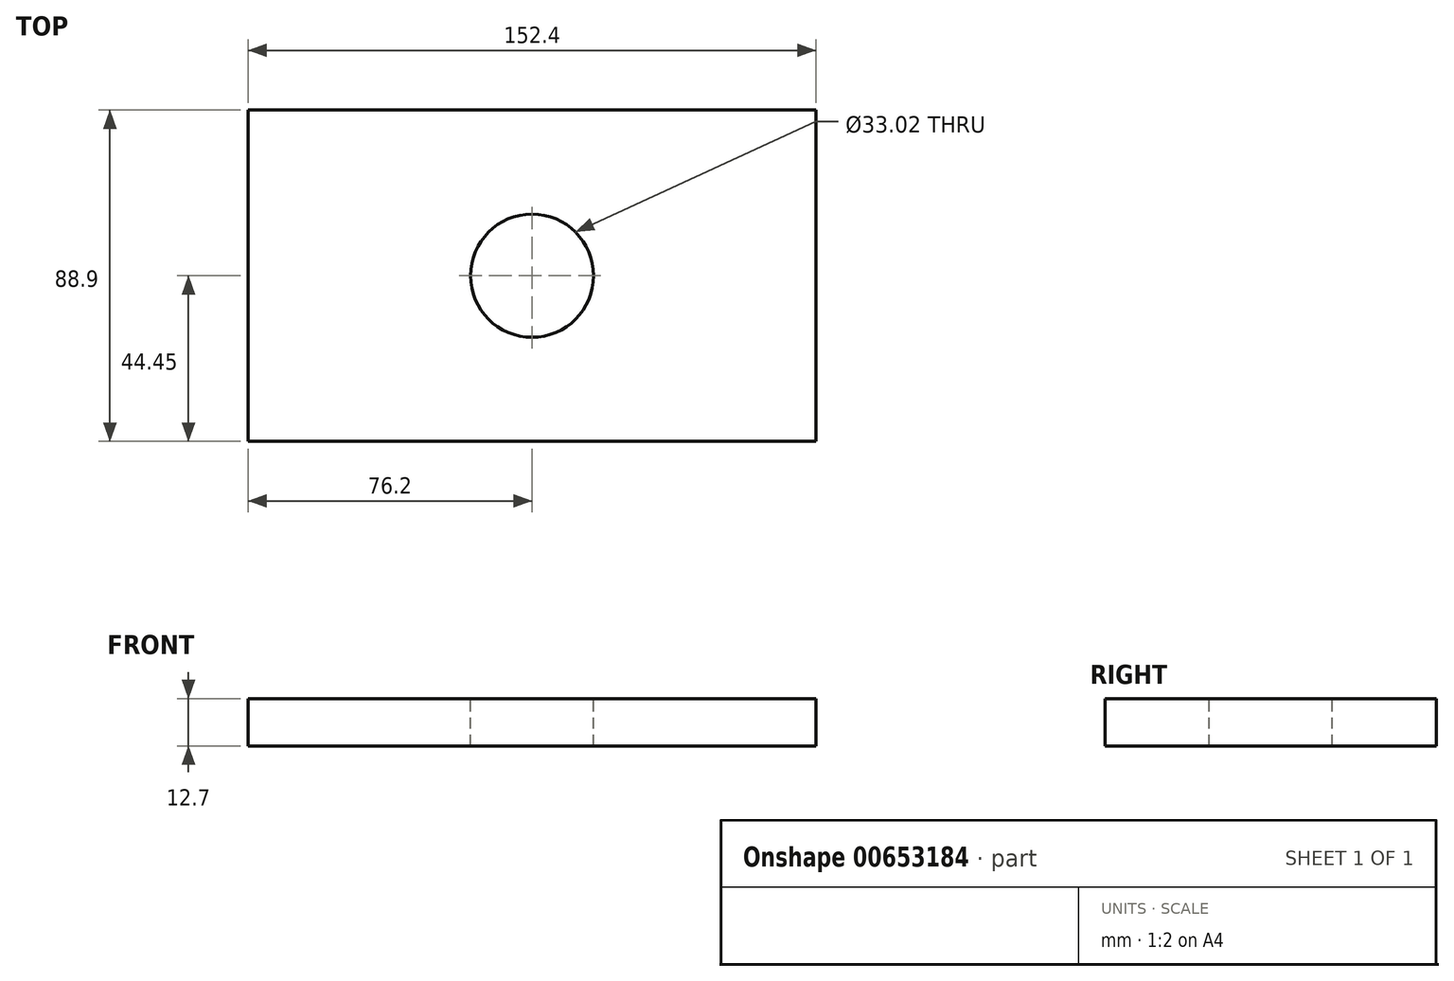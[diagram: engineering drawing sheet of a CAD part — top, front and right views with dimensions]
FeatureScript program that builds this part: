
annotation { "Feature Type Name" : "Feature", "Feature Type Description" : "" }
export const myFeature = defineFeature(function(context is Context, id is Id, definition is map)
    precondition{}
    {
        {
            var Q0;
            Q0=qCreatedBy(makeId("Top.planeOp"),FACE);
            var sketch = newSketch(context, id + "F0", { "sketchPlane" : qUnion([Q0])});
            skLineSegment(sketch, "E0.bottom", {"start": v(-76.2, -44.45) * mm, "end": v(76.2, -44.45) * mm});
            skLineSegment(sketch, "E0.top", {"start": v(-76.2, 44.45) * mm, "end": v(76.2, 44.45) * mm});
            skLineSegment(sketch, "E0.left", {"start": v(-76.2, -44.45) * mm, "end": v(-76.2, 44.45) * mm});
            skLineSegment(sketch, "E0.right", {"start": v(76.2, -44.45) * mm, "end": v(76.2, 44.45) * mm});
            skPoint(sketch, "E0.middle", {"position": v(0, 0) * mm});
            skCircle(sketch, "E1", {"center": v(0, 0) * mm, "radius": 16.51 * mm});
            skSolve(sketch);
        }
        {
            var Q0;
            Q0=makeQuery(id+"F0.imprint","IMPRINT",FACE,{"disambiguationData":[TD([[makeQuery(id+"F0.imprint","IMPRINT",EDGE,{"derivedFrom":sQuery(id+"F0.wireOp",EDGE,"E0.bottom")}),1.0]])]});
            extrude(context, id + "F1", {"entities" : qUnion([Q0]), "oppositeDirection" : true, "depth" : 12.7 * mm, "offsetDistance" : 25.4 * mm});
        }
    });
